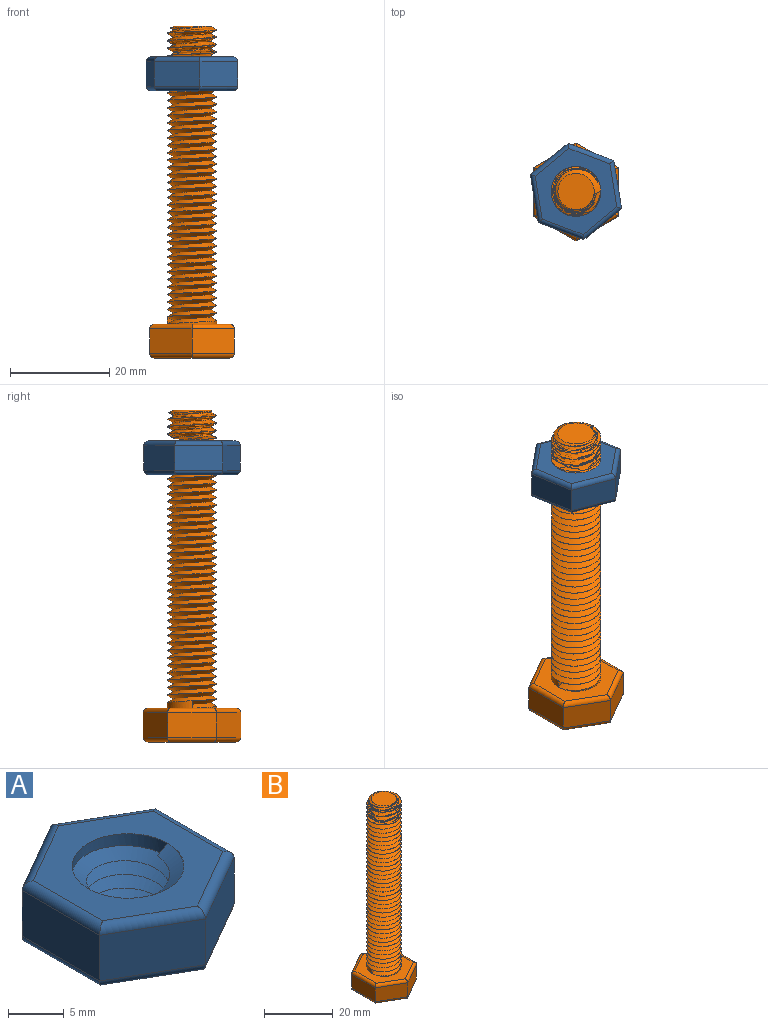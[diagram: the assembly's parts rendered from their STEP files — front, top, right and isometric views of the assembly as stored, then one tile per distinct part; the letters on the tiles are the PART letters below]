
ASSEMBLY  parts=2 mates=1
PART A: 24 faces, bbox 18.1x20.7x8.8 mm
  f0: bspline ~11.55x10mm, area 175.4mm2, adj f1,f8,f10,f11
  f1: bspline ~11.55x10mm, area 154.3mm2, adj f0,f8,f10,f11
  f2: plane 9.82x5mm, normal (-1,0,0), area 49.1mm2, adj f3,f7,f15,f21
  f3: plane 8.5x5mm, normal (-0.5,-0.87,0), area 49.1mm2, adj f2,f4,f13,f19
  f4: plane 8.5x5mm, normal (0.5,-0.87,0), area 49.1mm2, adj f3,f5,f12,f18
  f5: plane 9.82x5mm, normal (1,0,0), area 49.1mm2, adj f4,f6,f14,f20
  f6: plane 8.5x5mm, normal (0.5,0.87,0), area 49.1mm2, adj f5,f7,f16,f22
  f7: plane 8.5x5mm, normal (-0.5,0.87,0), area 49.1mm2, adj f2,f6,f17,f23
  f8: cylinder r=5mm len=10mm, axis (0,0,-1), area 25.3mm2, adj f0,f1,f9,f10,f11
  f9: plane 17.55x15.2mm, normal (0,0,1), area 121.5mm2, adj f8,f18,f19,f20,f21,f22,f23
  f10: plane 18.64x16.29mm, normal (0,0,-1), area 139.9mm2, adj f0,f1,f8,f12,f13,f14,f15,f16
  f11: plane 1.49x1.29mm, normal (0,1,0), area 1mm2, adj f0,f1,f8
  f12: cylinder r=0.9mm len=8.95mm, axis (0.87,0.5,0), area 13.1mm2, adj f4,f10,f13,f14
  f13: cylinder r=0.9mm len=8.95mm, axis (0.87,-0.5,0), area 13.1mm2, adj f3,f10,f12,f15
  f14: cylinder r=0.9mm len=9.82mm, axis (0,1,0), area 13.1mm2, adj f5,f10,f12,f16
  f15: cylinder r=0.9mm len=9.82mm, axis (0,-1,0), area 13.1mm2, adj f2,f10,f13,f17
  f16: cylinder r=0.9mm len=8.95mm, axis (-0.87,0.5,0), area 13.1mm2, adj f6,f10,f14,f17
  f17: cylinder r=0.9mm len=8.95mm, axis (-0.87,-0.5,0), area 13.1mm2, adj f7,f10,f15,f16
  f18: cylinder r=0.9mm len=8.95mm, axis (-0.87,-0.5,0), area 13.1mm2, adj f4,f9,f19,f20
  f19: cylinder r=0.9mm len=8.95mm, axis (-0.87,0.5,0), area 13.1mm2, adj f3,f9,f18,f21
  f20: cylinder r=0.9mm len=9.82mm, axis (0,-1,0), area 13.1mm2, adj f5,f9,f18,f22
  f21: cylinder r=0.9mm len=9.82mm, axis (0,1,0), area 13.1mm2, adj f2,f9,f19,f23
  f22: cylinder r=0.9mm len=8.95mm, axis (0.87,-0.5,0), area 13.1mm2, adj f6,f9,f20,f23
  f23: cylinder r=0.9mm len=8.95mm, axis (0.87,0.5,0), area 13.1mm2, adj f7,f9,f21,f22
PART B: 26 faces, bbox 17x19.6x67.5 mm
  f0: cone r=3.65mm half-angle=60.9deg, axis (0,0,-1), area 20.9mm2, adj f9,f10,f12,f13
  f1: plane 9.82x5mm, normal (-1,0,0), area 49.1mm2, adj f2,f6,f15,f21
  f2: plane 8.5x5mm, normal (-0.5,-0.87,0), area 49.1mm2, adj f1,f3,f14,f20
  f3: plane 8.5x5mm, normal (0.5,-0.87,0), area 49.1mm2, adj f2,f4,f16,f22
  f4: plane 9.82x5mm, normal (1,0,0), area 49.1mm2, adj f3,f5,f18,f24
  f5: plane 8.5x5mm, normal (0.5,0.87,0), area 49.1mm2, adj f4,f6,f19,f25
  f6: plane 8.5x5mm, normal (-0.5,0.87,0), area 49.1mm2, adj f1,f5,f17,f23
  f7: plane 17.55x15.2mm, normal (0,0,1), area 121.5mm2, adj f9,f20,f21,f22,f23,f24,f25
  f8: plane 17.55x15.2mm, normal (0,0,-1), area 200.1mm2, adj f14,f15,f16,f17,f18,f19
  f9: cylinder r=5mm len=59.25mm, axis (0,0,-1), area 1482.2mm2, adj f0,f7,f11,f12,f13
  f10: plane 7.3x7.3mm, normal (0,0,1), area 41.9mm2, adj f0
  f11: plane 1.49x1.29mm, normal (0,-1,0), area 1mm2, adj f9,f12,f13
  f12: bspline ~60.25x11.55mm, area 1624.4mm2, adj f0,f9,f11,f13
  f13: bspline ~60x11.55mm, area 1584.8mm2, adj f0,f9,f11,f12
  f14: cylinder r=0.9mm len=8.95mm, axis (0.87,-0.5,0), area 13.1mm2, adj f2,f8,f15,f16
  f15: cylinder r=0.9mm len=9.82mm, axis (0,-1,0), area 13.1mm2, adj f1,f8,f14,f17
  f16: cylinder r=0.9mm len=8.95mm, axis (0.87,0.5,0), area 13.1mm2, adj f3,f8,f14,f18
  f17: cylinder r=0.9mm len=8.95mm, axis (-0.87,-0.5,0), area 13.1mm2, adj f6,f8,f15,f19
  f18: cylinder r=0.9mm len=9.82mm, axis (0,1,0), area 13.1mm2, adj f4,f8,f16,f19
  f19: cylinder r=0.9mm len=8.95mm, axis (-0.87,0.5,0), area 13.1mm2, adj f5,f8,f17,f18
  f20: cylinder r=0.9mm len=8.95mm, axis (-0.87,0.5,0), area 13.1mm2, adj f2,f7,f21,f22
  f21: cylinder r=0.9mm len=9.82mm, axis (0,1,0), area 13.1mm2, adj f1,f7,f20,f23
  f22: cylinder r=0.9mm len=8.95mm, axis (-0.87,-0.5,0), area 13.1mm2, adj f3,f7,f20,f24
  f23: cylinder r=0.9mm len=8.95mm, axis (0.87,0.5,0), area 13.1mm2, adj f6,f7,f21,f25
  f24: cylinder r=0.9mm len=9.82mm, axis (0,-1,0), area 13.1mm2, adj f4,f7,f22,f25
  f25: cylinder r=0.9mm len=8.95mm, axis (0.87,-0.5,0), area 13.1mm2, adj f5,f7,f23,f24
PLACE A rot(axis=(0,0,-1),170.6deg) t=(-71.95,-2.67,10.17)mm
PLACE B t=(-33.58,3.68,-43.6)mm fixed
MATE cylindrical B.f0 <-> A.f8  axis (0,0,1) through (-33.58,3.68,23.2)mm
